# Revit family: QF_BOURGEAT_Rayonnage_modulaire_étagère_retour_Polypropylène
name_source: partatom
category: Equipement spécialisé
revit_build: Autodesk Revit 2015 (Build: 20140606_1530(x64)
units: mm (PartAtom-declared; Revit-internal decimal feet)

## types (1)
- QF_BOURGEAT_Rayonnage_modulaire_étagère_retour_Polypropylène
    4 niveaux = Oui
    4 niveaux Plateau 2 = Oui
    4 niveaux plateau 3 = Oui
    Calagepl2 = 1151 mm
    Calagepl3 = 2302 mm
    CentPl1 = 576 mm
    CentPl2 = 576 mm
    CentPl3 = 631 mm
    Certification = NF hygiene alimentaire
    Clayette = Acier inoxydable
    Epaisseur de retour = 415 mm  [stored 1.36155 ft]
    Fabricant = BOURGEAT
    Hauteur hors tout = 1730 mm  [stored 5.67585 ft]
    Jeu = 174 mm
    LP1 = 4
    LP2 = 4
    LP3 = 5
    Longeron = Acier inoxydable
    Longueur = 4010 mm
    Longueur Plateau 1 = 1083 mm  [stored 3.55315 ft]
    Longueur Plateau 2 = 1083 mm  [stored 3.55315 ft]
    Longueur Plateau 3 = 1191 mm  [stored 3.90748 ft]
    Longueur entraxe 1 = 1093 mm
    Longueur entraxe 2 = 1093 mm
    Longueur entraxe 3 = 1203 mm
    Longueur hors tout = 4010 mm
    Longueur longeron 1 = 1125 mm  [stored 3.69094 ft]
    Longueur longeron 2 = 1125 mm  [stored 3.69094 ft]
    Longueur longeron 3 = 1230 mm  [stored 4.03543 ft]
    Longueur retour = 3595 mm
    Plateau 2 = Oui
    Plateau 3 = Oui
    Profondeur = 425 mm  [stored 1.39436 ft]
    Profondeur hors tout = 425 mm  [stored 1.39436 ft]
    Type article = Etagères de Base clayette polypropylène
    URL catalogue = http://www.bourgeat.fr

note: [stored X ft] marks values corroborated as IEEE doubles in the binary element streams (Revit-internal decimal feet)
